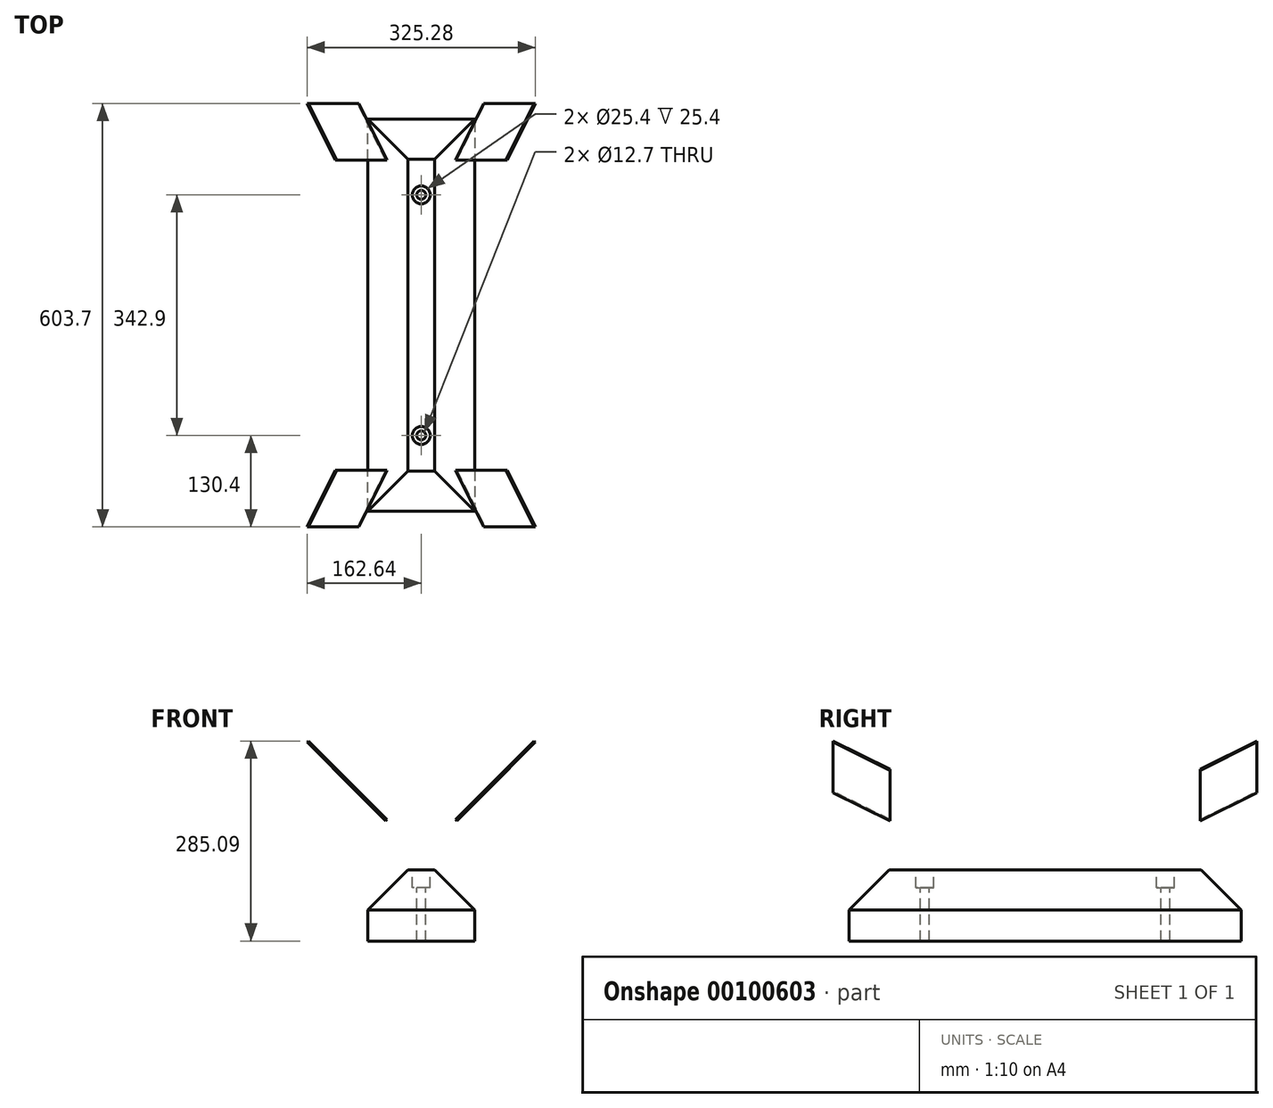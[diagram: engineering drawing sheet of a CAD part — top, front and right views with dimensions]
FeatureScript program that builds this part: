
annotation { "Feature Type Name" : "Feature", "Feature Type Description" : "" }
export const myFeature = defineFeature(function(context is Context, id is Id, definition is map)
    precondition{}
    {
        {
            var Q0;
            Q0=qCreatedBy(makeId("Front.planeOp"),FACE);
            var sketch = newSketch(context, id + "F0", { "sketchPlane" : qUnion([Q0])});
            skLineSegment(sketch, "E0.bottom", {"start": v(76.2, -50.8) * mm, "end": v(-76.2, -50.8) * mm});
            skLineSegment(sketch, "E0.top", {"start": v(76.2, 50.8) * mm, "end": v(-76.2, 50.8) * mm});
            skLineSegment(sketch, "E0.left", {"start": v(76.2, -50.8) * mm, "end": v(76.2, 50.8) * mm});
            skLineSegment(sketch, "E0.right", {"start": v(-76.2, -50.8) * mm, "end": v(-76.2, 50.8) * mm});
            skSolve(sketch);
        }
        {
            var Q0;
            Q0 = qSketchRegion(id + "F0", true);
            extrude(context, id + "F1", {"entities" : qUnion([Q0]), "oppositeDirection" : true, "depth" : 558.8 * mm});
        }
        {
            var Q0;
            Q0=makeQuery(id+"F1.opExtrude","SWEPT_EDGE",EDGE,{"disambiguationData":[OSD([sQuery(id+"F0.wireOp",EDGE,"E0.top"),sQuery(id+"F0.wireOp",EDGE,"E0.left")])]});
            var Q1;
            Q1=makeQuery(id+"F1.opExtrude","CAP_EDGE",EDGE,{"disambiguationData":[OSD([sQuery(id+"F0.wireOp",EDGE,"E0.top")])],"isStart":true});
            var Q2;
            Q2=makeQuery(id+"F1.opExtrude","SWEPT_EDGE",EDGE,{"disambiguationData":[OSD([sQuery(id+"F0.wireOp",EDGE,"E0.top"),sQuery(id+"F0.wireOp",EDGE,"E0.right")])]});
            var Q3;
            Q3=makeQuery(id+"F1.opExtrude","CAP_EDGE",EDGE,{"disambiguationData":[OSD([sQuery(id+"F0.wireOp",EDGE,"E0.top")])],"isStart":false});
            chamfer(context, id + "F2", {"entities" : qUnion([Q0, Q1, Q2, Q3]), "width" : 57.15 * mm, "tangentPropagation" : true});
        }
        {
            var Q0;
            Q0=qCreatedBy(makeId("Front.planeOp"),FACE);
            cPlane(context, id + "F3", {"entities" : qUnion([Q0]), "cplaneType" : CPlaneType.OFFSET, "offset" : 279.4 * mm, "oppositeDirection" : true, "width" : 152.4 * mm, "height" : 152.4 * mm});
        }
        {
            var Q0;
            Q0=makeQuery(id+"F2.opChamfer","BLEND_FACE",FACE,{"disambiguationData":[OSD([sQuery(id+"F0.wireOp",EDGE,"E0.top"),sQuery(id+"F0.wireOp",EDGE,"E0.left")])]});
            var sketch = newSketch(context, id + "F4", { "sketchPlane" : qUnion([Q0])});
            skLineSegment(sketch, "E1", {"start": v(-22.45, 279.4) * mm, "end": v(58.37, 222.8) * mm});
            skLineSegment(sketch, "E2", {"start": v(58.37, 222.8) * mm, "end": v(58.37, 121.2) * mm});
            skLineSegment(sketch, "E3", {"start": v(58.37, 121.2) * mm, "end": v(-22.45, 177.8) * mm});
            skLineSegment(sketch, "E4", {"start": v(-22.45, 177.8) * mm, "end": v(-22.45, 279.4) * mm});
            skSolve(sketch);
        }
        {
            var Q0;
            Q0=makeQuery(id+"F4.imprint","IMPRINT",FACE,{"disambiguationData":[TD([[makeQuery(id+"F4.imprint","IMPRINT",EDGE,{"derivedFrom":sQuery(id+"F4.wireOp",EDGE,"E1")}),-1.0]])]});
            extrude(context, id + "F5", {"entities" : qUnion([Q0]), "depth" : 2.54 * mm});
        }
        {
            var Q0;
            Q0=makeQuery(id+"F5.opExtrude","SWEPT_BODY",BODY,{"disambiguationData":[OSD([sQuery(id+"F4.wireOp",EDGE,"E1"),sQuery(id+"F4.wireOp",EDGE,"E2"),sQuery(id+"F4.wireOp",EDGE,"E3"),sQuery(id+"F4.wireOp",EDGE,"E4")])]});
            var Q1;
            Q1=qCreatedBy(id+"F3.planeOp",FACE);
            mirror(context, id + "F6", {"entities" : qUnion([Q0]), "mirrorPlane" : qUnion([Q1])});
        }
        {
            var Q0;
            Q0=makeQuery(id+"F5.opExtrude","SWEPT_BODY",BODY,{"disambiguationData":[OSD([sQuery(id+"F4.wireOp",EDGE,"E1"),sQuery(id+"F4.wireOp",EDGE,"E2"),sQuery(id+"F4.wireOp",EDGE,"E3"),sQuery(id+"F4.wireOp",EDGE,"E4")])]});
            var Q1;
            Q1=makeQuery(id+"F6.opPattern","COPY",BODY,{"derivedFrom":makeQuery(id+"F5.opExtrude","SWEPT_BODY",BODY,{"disambiguationData":[OSD([sQuery(id+"F4.wireOp",EDGE,"E1"),sQuery(id+"F4.wireOp",EDGE,"E2"),sQuery(id+"F4.wireOp",EDGE,"E3"),sQuery(id+"F4.wireOp",EDGE,"E4")])]}),"instanceName":"1"});
            var Q2;
            Q2=qCreatedBy(makeId("Right.planeOp"),FACE);
            mirror(context, id + "F7", {"entities" : qUnion([Q0, Q1]), "mirrorPlane" : qUnion([Q2])});
        }
        {
            var Q0;
            Q0=makeQuery(id+"F1.opExtrude","SWEPT_FACE",FACE,{"disambiguationData":[OSD([sQuery(id+"F0.wireOp",EDGE,"E0.top")])]});
            var sketch = newSketch(context, id + "F8", { "sketchPlane" : qUnion([Q0])});
            skCircle(sketch, "E5", {"center": v(0, 107.95) * mm, "radius": 12.7 * mm});
            skCircle(sketch, "E6", {"center": v(0, 450.85) * mm, "radius": 12.7 * mm});
            skCircle(sketch, "E7", {"center": v(0, 107.95) * mm, "radius": 6.35 * mm});
            skCircle(sketch, "E8", {"center": v(0, 450.85) * mm, "radius": 6.35 * mm});
            skSolve(sketch);
        }
        {
            var Q0;
            Q0 = qSketchRegion(id + "F8", true);
            extrude(context, id + "F9", {"entities" : qUnion([Q0]), "operationType" : NewBodyOperationType.REMOVE, "oppositeDirection" : true, "depth" : 25.4 * mm});
        }
        {
            var Q0;
            Q0=makeQuery(id+"F9.boolean.opBoolean","SPLIT",FACE,{"disambiguationData":[TD([makeQuery(id+"F9.opExtrude","SWEPT_FACE",FACE,{"disambiguationData":[OSD([sQuery(id+"F8.wireOp",EDGE,"E7")])]})])],"derivedFrom":makeQuery(id+"F1.opExtrude","SWEPT_FACE",FACE,{"disambiguationData":[OSD([sQuery(id+"F0.wireOp",EDGE,"E0.top")])]})});
            var Q1;
            Q1=makeQuery(id+"F9.boolean.opBoolean","SPLIT",FACE,{"disambiguationData":[TD([makeQuery(id+"F9.opExtrude","SWEPT_FACE",FACE,{"disambiguationData":[OSD([sQuery(id+"F8.wireOp",EDGE,"E8")])]})])],"derivedFrom":makeQuery(id+"F1.opExtrude","SWEPT_FACE",FACE,{"disambiguationData":[OSD([sQuery(id+"F0.wireOp",EDGE,"E0.top")])]})});
            extrude(context, id + "F10", {"entities" : qUnion([Q0, Q1]), "operationType" : NewBodyOperationType.REMOVE, "endBound" : BoundingType.THROUGH_ALL, "oppositeDirection" : true, "depth" : 25.4 * mm});
        }
    });
